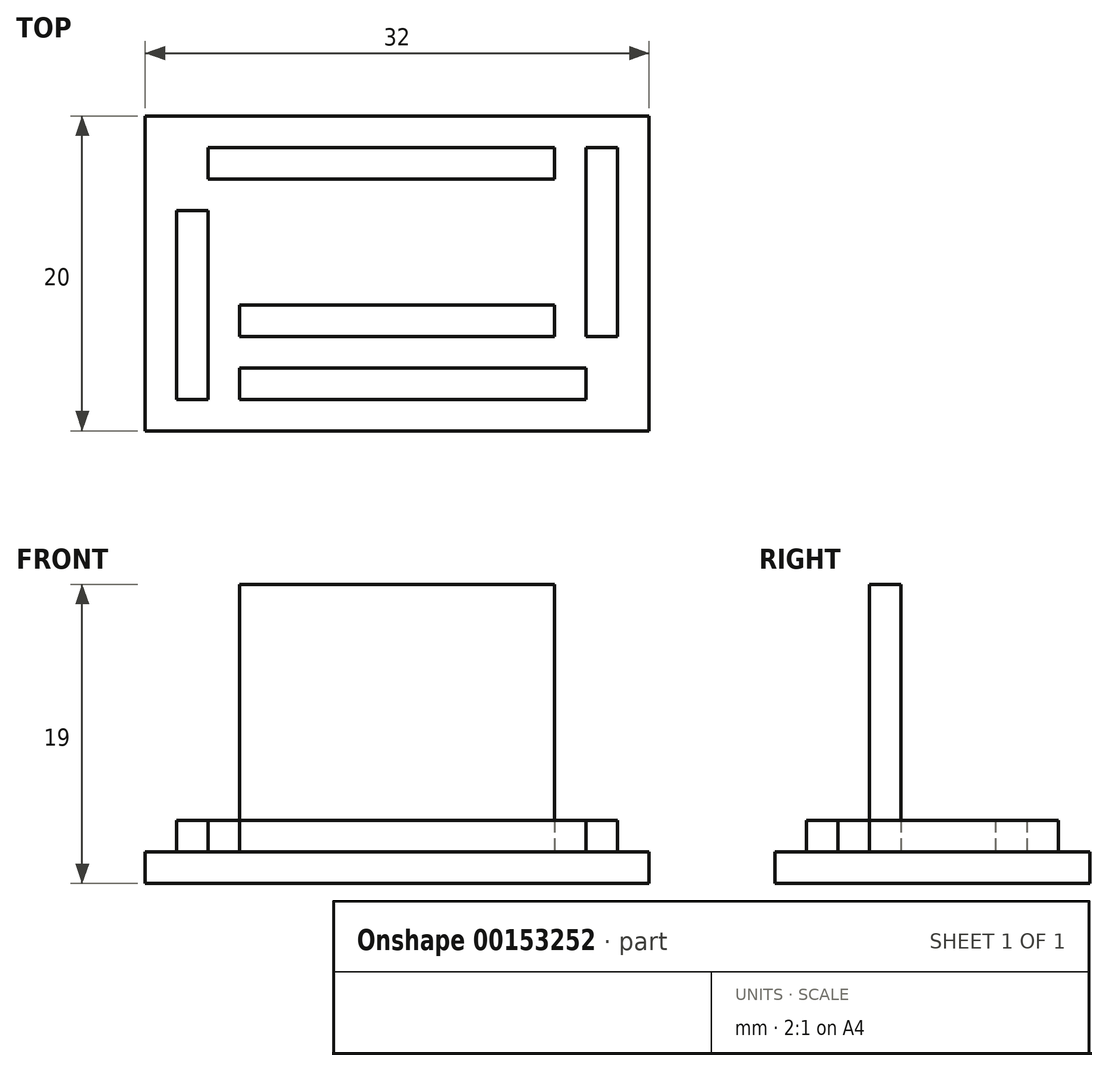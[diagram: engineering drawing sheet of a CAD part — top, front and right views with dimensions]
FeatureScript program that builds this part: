
annotation { "Feature Type Name" : "Feature", "Feature Type Description" : "" }
export const myFeature = defineFeature(function(context is Context, id is Id, definition is map)
    precondition{}
    {
        {
            assignVariable(context, id + "F0", {"name" : "T", "anyValue" : 2});
        }
        {
            var Q0;
            Q0=qCreatedBy(makeId("Top.planeOp"),FACE);
            var sketch = newSketch(context, id + "F1", { "sketchPlane" : qUnion([Q0])});
            skLineSegment(sketch, "E0.bottom", {"start": v(16, -10) * mm, "end": v(-16, -10) * mm});
            skLineSegment(sketch, "E0.top", {"start": v(16, 10) * mm, "end": v(-16, 10) * mm});
            skLineSegment(sketch, "E0.left", {"start": v(16, -10) * mm, "end": v(16, 10) * mm});
            skLineSegment(sketch, "E0.right", {"start": v(-16, -10) * mm, "end": v(-16, 10) * mm});
            skPoint(sketch, "E0.middle", {"position": v(0, 0) * mm});
            skSolve(sketch);
        }
        {
            var Q0;
            Q0=makeQuery(id+"F1.imprint","IMPRINT",FACE,{"disambiguationData":[TD([[makeQuery(id+"F1.imprint","IMPRINT",EDGE,{"derivedFrom":sQuery(id+"F1.wireOp",EDGE,"E0.bottom")}),-1.0]])]});
            extrude(context, id + "F2", {"entities" : qUnion([Q0]), "depth" : (getVariable(context, 'T')) * mm});
        }
        {
            var Q0;
            Q0=makeQuery(id+"F2.opExtrude","CAP_FACE",FACE,{"disambiguationData":[OSD([sQuery(id+"F1.wireOp",EDGE,"E0.bottom"),sQuery(id+"F1.wireOp",EDGE,"E0.top"),sQuery(id+"F1.wireOp",EDGE,"E0.left"),sQuery(id+"F1.wireOp",EDGE,"E0.right")])],"isStart":false});
            var sketch = newSketch(context, id + "F3", { "sketchPlane" : qUnion([Q0])});
            skLineSegment(sketch, "E1.0", {"start": v(14, 8) * mm, "end": v(-14, 8) * mm, "construction": true});
            skLineSegment(sketch, "E1.1", {"start": v(14, -8) * mm, "end": v(14, 8) * mm, "construction": true});
            skLineSegment(sketch, "E1.2", {"start": v(14, -8) * mm, "end": v(-14, -8) * mm, "construction": true});
            skLineSegment(sketch, "E1.3", {"start": v(-14, -8) * mm, "end": v(-14, 8) * mm, "construction": true});
            skLineSegment(sketch, "E2.bottom", {"start": v(-14, -8) * mm, "end": v(-12, -8) * mm});
            skLineSegment(sketch, "E2.top", {"start": v(-14, 4) * mm, "end": v(-12, 4) * mm});
            skLineSegment(sketch, "E2.left", {"start": v(-14, -8) * mm, "end": v(-14, 4) * mm});
            skLineSegment(sketch, "E2.right", {"start": v(-12, -8) * mm, "end": v(-12, 4) * mm});
            skLineSegment(sketch, "E3.bottom", {"start": v(14, 8) * mm, "end": v(12, 8) * mm});
            skLineSegment(sketch, "E3.top", {"start": v(14, -4) * mm, "end": v(12, -4) * mm});
            skLineSegment(sketch, "E3.left", {"start": v(14, 8) * mm, "end": v(14, -4) * mm});
            skLineSegment(sketch, "E3.right", {"start": v(12, 8) * mm, "end": v(12, -4) * mm});
            skLineSegment(sketch, "E4.bottom", {"start": v(-12, 8) * mm, "end": v(10, 8) * mm});
            skLineSegment(sketch, "E4.top", {"start": v(-12, 6) * mm, "end": v(10, 6) * mm});
            skLineSegment(sketch, "E4.left", {"start": v(-12, 8) * mm, "end": v(-12, 6) * mm});
            skLineSegment(sketch, "E4.right", {"start": v(10, 8) * mm, "end": v(10, 6) * mm});
            skLineSegment(sketch, "E5.bottom", {"start": v(12, -8) * mm, "end": v(-10, -8) * mm});
            skLineSegment(sketch, "E5.top", {"start": v(12, -6) * mm, "end": v(-10, -6) * mm});
            skLineSegment(sketch, "E5.left", {"start": v(12, -8) * mm, "end": v(12, -6) * mm});
            skLineSegment(sketch, "E5.right", {"start": v(-10, -8) * mm, "end": v(-10, -6) * mm});
            skSolve(sketch);
        }
        {
            var Q0;
            Q0=makeQuery(id+"F3.imprint","IMPRINT",FACE,{"disambiguationData":[TD([[makeQuery(id+"F3.imprint","IMPRINT",EDGE,{"derivedFrom":sQuery(id+"F3.wireOp",EDGE,"E4.bottom")}),-1.0]])]});
            var Q1;
            Q1=makeQuery(id+"F3.imprint","IMPRINT",FACE,{"disambiguationData":[TD([[makeQuery(id+"F3.imprint","IMPRINT",EDGE,{"derivedFrom":sQuery(id+"F3.wireOp",EDGE,"E3.bottom")}),1.0]])]});
            var Q2;
            Q2=makeQuery(id+"F3.imprint","IMPRINT",FACE,{"disambiguationData":[TD([[makeQuery(id+"F3.imprint","IMPRINT",EDGE,{"derivedFrom":sQuery(id+"F3.wireOp",EDGE,"E5.bottom")}),-1.0]])]});
            var Q3;
            Q3=makeQuery(id+"F3.imprint","IMPRINT",FACE,{"disambiguationData":[TD([[makeQuery(id+"F3.imprint","IMPRINT",EDGE,{"derivedFrom":sQuery(id+"F3.wireOp",EDGE,"E2.bottom")}),1.0]])]});
            extrude(context, id + "F4", {"entities" : qUnion([Q0, Q1, Q2, Q3]), "operationType" : NewBodyOperationType.ADD, "depth" : (getVariable(context, 'T')) * mm});
        }
        {
            var Q0;
            Q0=makeQuery(id+"F2.opExtrude","CAP_FACE",FACE,{"disambiguationData":[OSD([sQuery(id+"F1.wireOp",EDGE,"E0.bottom"),sQuery(id+"F1.wireOp",EDGE,"E0.top"),sQuery(id+"F1.wireOp",EDGE,"E0.left"),sQuery(id+"F1.wireOp",EDGE,"E0.right")])],"isStart":false});
            var sketch = newSketch(context, id + "F5", { "sketchPlane" : qUnion([Q0])});
            skLineSegment(sketch, "E6.bottom", {"start": v(10, 4) * mm, "end": v(-10, 4) * mm, "construction": true});
            skLineSegment(sketch, "E6.top", {"start": v(10, -4) * mm, "end": v(-10, -4) * mm, "construction": true});
            skLineSegment(sketch, "E6.left", {"start": v(10, 4) * mm, "end": v(10, -4) * mm, "construction": true});
            skLineSegment(sketch, "E6.right", {"start": v(-10, 4) * mm, "end": v(-10, -4) * mm, "construction": true});
            skPoint(sketch, "E6.middle", {"position": v(0, 0) * mm});
            skLineSegment(sketch, "E7.bottom", {"start": v(-10, -4) * mm, "end": v(10, -4) * mm});
            skLineSegment(sketch, "E7.top", {"start": v(-10, -2) * mm, "end": v(10, -2) * mm});
            skLineSegment(sketch, "E7.left", {"start": v(-10, -4) * mm, "end": v(-10, -2) * mm});
            skLineSegment(sketch, "E7.right", {"start": v(10, -4) * mm, "end": v(10, -2) * mm});
            skLineSegment(sketch, "E8.bottom", {"start": v(10, -2) * mm, "end": v(8, -2) * mm});
            skLineSegment(sketch, "E8.top", {"start": v(10, 4) * mm, "end": v(8, 4) * mm});
            skLineSegment(sketch, "E8.left", {"start": v(10, -2) * mm, "end": v(10, 4) * mm});
            skLineSegment(sketch, "E8.right", {"start": v(8, -2) * mm, "end": v(8, 4) * mm});
            skLineSegment(sketch, "E9.bottom", {"start": v(-10, -2) * mm, "end": v(-8, -2) * mm});
            skLineSegment(sketch, "E9.top", {"start": v(-10, 4) * mm, "end": v(-8, 4) * mm});
            skLineSegment(sketch, "E9.left", {"start": v(-10, -2) * mm, "end": v(-10, 4) * mm});
            skLineSegment(sketch, "E9.right", {"start": v(-8, -2) * mm, "end": v(-8, 4) * mm});
            skSolve(sketch);
        }
        {
            var Q0;
            Q0=makeQuery(id+"F5.imprint","IMPRINT",FACE,{"disambiguationData":[TD([[makeQuery(id+"F5.imprint","IMPRINT",EDGE,{"derivedFrom":sQuery(id+"F5.wireOp",EDGE,"E9.bottom")}),1.0]])]});
            var Q1;
            Q1=makeQuery(id+"F5.imprint","IMPRINT",FACE,{"disambiguationData":[TD([[makeQuery(id+"F5.imprint","IMPRINT",EDGE,{"derivedFrom":sQuery(id+"F5.wireOp",EDGE,"E7.bottom")}),1.0]])]});
            var Q2;
            Q2=makeQuery(id+"F5.imprint","IMPRINT",FACE,{"disambiguationData":[TD([[makeQuery(id+"F5.imprint","IMPRINT",EDGE,{"derivedFrom":sQuery(id+"F5.wireOp",EDGE,"E8.bottom")}),-1.0]])]});
            extrude(context, id + "F6", {"entities" : qUnion([Q0, Q1, Q2]), "operationType" : NewBodyOperationType.ADD, "depth" : (8 * getVariable(context, 'T') + 1) * mm});
        }
    });
